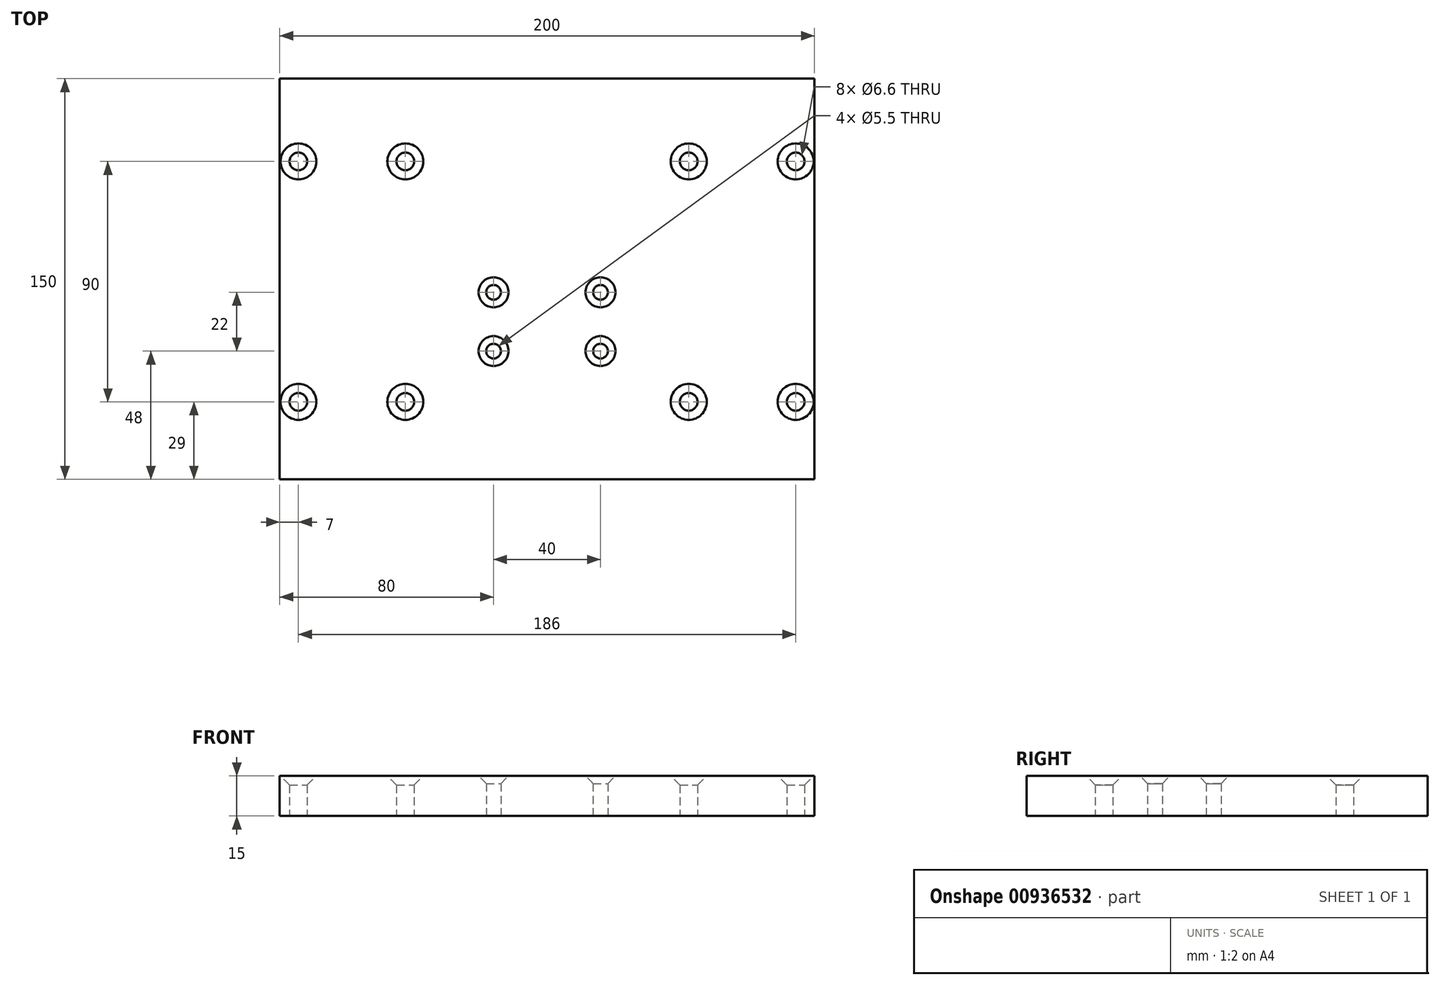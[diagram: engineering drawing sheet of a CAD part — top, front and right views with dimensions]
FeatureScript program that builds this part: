
annotation { "Feature Type Name" : "Feature", "Feature Type Description" : "" }
export const myFeature = defineFeature(function(context is Context, id is Id, definition is map)
    precondition{}
    {
        {
            var Q0;
            Q0=qCreatedBy(makeId("Top.planeOp"),FACE);
            var sketch = newSketch(context, id + "F0", { "sketchPlane" : qUnion([Q0])});
            skLineSegment(sketch, "E0.bottom", {"start": v(100, 75) * mm, "end": v(-100, 75) * mm});
            skLineSegment(sketch, "E0.top", {"start": v(100, -75) * mm, "end": v(-100, -75) * mm});
            skLineSegment(sketch, "E0.left", {"start": v(100, 75) * mm, "end": v(100, -75) * mm});
            skLineSegment(sketch, "E0.right", {"start": v(-100, 75) * mm, "end": v(-100, -75) * mm});
            skPoint(sketch, "E0.middle", {"position": v(0, 0) * mm});
            skSolve(sketch);
        }
        {
            var Q0;
            Q0 = qSketchRegion(id + "F0", true);
            extrude(context, id + "F1", {"entities" : qUnion([Q0]), "depth" : 15 * mm, "offsetDistance" : 25 * mm});
        }
        {
            var Q0;
            Q0=makeQuery(id+"F1.opExtrude","CAP_FACE",FACE,{"disambiguationData":[OSD([sQuery(id+"F0.wireOp",EDGE,"E0.bottom"),sQuery(id+"F0.wireOp",EDGE,"E0.top"),sQuery(id+"F0.wireOp",EDGE,"E0.left"),sQuery(id+"F0.wireOp",EDGE,"E0.right")])],"isStart":false});
            var sketch = newSketch(context, id + "F2", { "sketchPlane" : qUnion([Q0])});
            skPoint(sketch, "E1", {"position": v(-93, 44) * mm});
            skPoint(sketch, "E2", {"position": v(-53, 44) * mm});
            skPoint(sketch, "E3", {"position": v(-93, -46) * mm});
            skPoint(sketch, "E4", {"position": v(-53, -46) * mm});
            skPoint(sketch, "E5.MirrorP", {"position": v(93, 44) * mm});
            skPoint(sketch, "E6.MirrorP", {"position": v(53, 44) * mm});
            skPoint(sketch, "E7.MirrorP", {"position": v(93, -46) * mm});
            skPoint(sketch, "E8.MirrorP", {"position": v(53, -46) * mm});
            skPoint(sketch, "E9", {"position": v(-20, -5) * mm});
            skPoint(sketch, "E10", {"position": v(-20, -27) * mm});
            skPoint(sketch, "E11.MirrorP", {"position": v(20, -5) * mm});
            skPoint(sketch, "E12.MirrorP", {"position": v(20, -27) * mm});
            skSolve(sketch);
        }
        {
            var Q0;
            Q0=sQuery(id+"F2.wireOp",VERTEX,"E1");
            var Q1;
            Q1=sQuery(id+"F2.wireOp",VERTEX,"E2");
            var Q2;
            Q2=sQuery(id+"F2.wireOp",VERTEX,"E3");
            var Q3;
            Q3=sQuery(id+"F2.wireOp",VERTEX,"E4");
            var Q4;
            Q4=sQuery(id+"F2.wireOp",VERTEX,"E6.MirrorP");
            var Q5;
            Q5=sQuery(id+"F2.wireOp",VERTEX,"E5.MirrorP");
            var Q6;
            Q6=sQuery(id+"F2.wireOp",VERTEX,"E8.MirrorP");
            var Q7;
            Q7=sQuery(id+"F2.wireOp",VERTEX,"E7.MirrorP");
            var Q8;
            Q8=makeQuery(id+"F1.opExtrude","SWEPT_BODY",BODY,{"disambiguationData":[OSD([sQuery(id+"F0.wireOp",EDGE,"E0.bottom"),sQuery(id+"F0.wireOp",EDGE,"E0.top"),sQuery(id+"F0.wireOp",EDGE,"E0.left"),sQuery(id+"F0.wireOp",EDGE,"E0.right")])]});
            hole(context, id + "F3", {"style" : HoleStyle.C_SINK, "endStyle" : HoleEndStyle.THROUGH, "standardTappedOrClearance" : lookupTablePath({ "fit" : "Normal", "standard" : "ISO", "size" : "M6", "type" : "Clearance" }), "standardBlindInLast" : lookupTablePath({ "fit" : "Normal", "standard" : "ISO", "engagement" : "75%", "pitch" : "1 mm", "size" : "M6", "type" : "Clearance & tapped" }), "holeDiameter" : 6.6 * mm, "cSinkDiameter" : 13.44 * mm, "cSinkAngle" : 90 * degree, "majorDiameter" : 5 * mm, "tappedDepth" : 12 * mm, "tapClearance" : 3, "locations" : qUnion([Q0, Q1, Q2, Q3, Q4, Q5, Q6, Q7]), "scope" : qUnion([Q8]), "startStyle" : HoleStartStyle.PART});
        }
        {
            var Q0;
            Q0=sQuery(id+"F2.wireOp",VERTEX,"E10");
            var Q1;
            Q1=sQuery(id+"F2.wireOp",VERTEX,"E9");
            var Q2;
            Q2=sQuery(id+"F2.wireOp",VERTEX,"E11.MirrorP");
            var Q3;
            Q3=sQuery(id+"F2.wireOp",VERTEX,"E12.MirrorP");
            var Q4;
            Q4=makeQuery(id+"F1.opExtrude","SWEPT_BODY",BODY,{"disambiguationData":[OSD([sQuery(id+"F0.wireOp",EDGE,"E0.bottom"),sQuery(id+"F0.wireOp",EDGE,"E0.top"),sQuery(id+"F0.wireOp",EDGE,"E0.left"),sQuery(id+"F0.wireOp",EDGE,"E0.right")])]});
            hole(context, id + "F4", {"style" : HoleStyle.C_SINK, "endStyle" : HoleEndStyle.THROUGH, "standardTappedOrClearance" : lookupTablePath({ "fit" : "Normal", "standard" : "ISO", "size" : "M5", "type" : "Clearance" }), "standardBlindInLast" : lookupTablePath({ "fit" : "Normal", "standard" : "ISO", "engagement" : "75%", "pitch" : "0.8 mm", "size" : "M5", "type" : "Clearance & tapped" }), "holeDiameter" : 5.5 * mm, "cSinkDiameter" : 11.2 * mm, "cSinkAngle" : 90 * degree, "majorDiameter" : 5 * mm, "tappedDepth" : 12 * mm, "tapClearance" : 3, "locations" : qUnion([Q0, Q1, Q2, Q3]), "scope" : qUnion([Q4]), "startStyle" : HoleStartStyle.PART});
        }
    });
